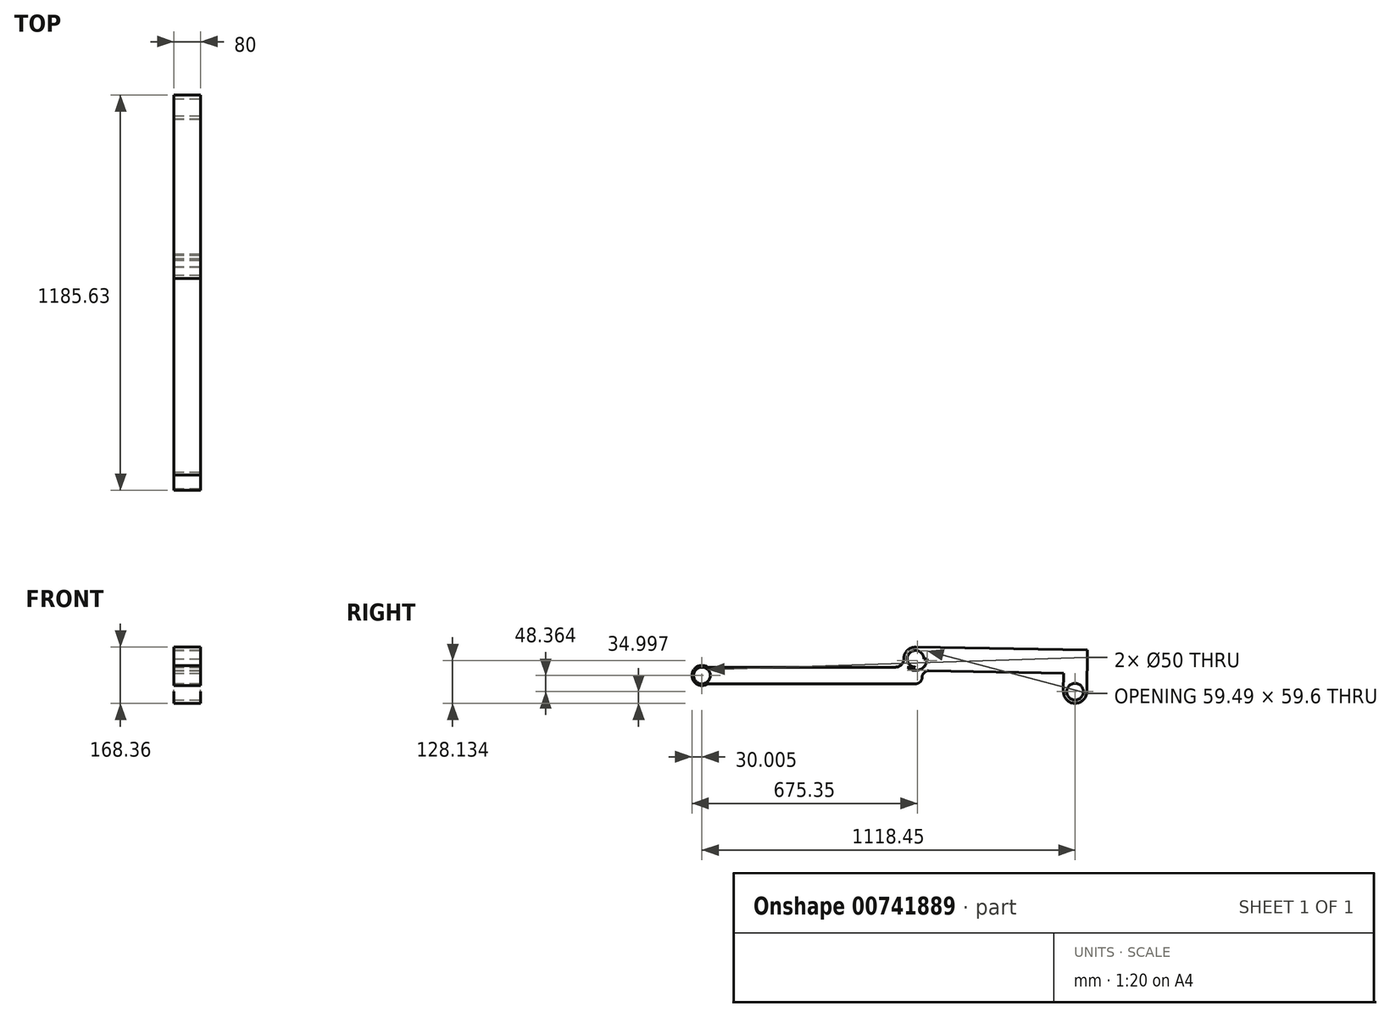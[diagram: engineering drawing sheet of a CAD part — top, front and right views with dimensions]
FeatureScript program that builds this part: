
annotation { "Feature Type Name" : "Feature", "Feature Type Description" : "" }
export const myFeature = defineFeature(function(context is Context, id is Id, definition is map)
    precondition{}
    {
        {
            var Q0;
            Q0=qCreatedBy(makeId("Right.planeOp"),FACE);
            var sketch = newSketch(context, id + "F0", { "sketchPlane" : qUnion([Q0])});
            skCircle(sketch, "E0", {"center": v(0, 0) * mm, "radius": 25 * mm});
            skLineSegment(sketch, "E1", {"start": v(0, -25) * mm, "end": v(-640, -25) * mm});
            skCircle(sketch, "E2", {"center": v(-640.1, -50) * mm, "radius": 25 * mm});
            skCircle(sketch, "E3", {"center": v(0, 0) * mm, "radius": 35 * mm});
            skArc(sketch, "E4", {"start": v(-35, 0) * mm, "mid": v(-42.32, -17.68) * mm, "end": v(-60, -25) * mm});
            skCircle(sketch, "E5", {"center": v(-640.1, -50) * mm, "radius": 30 * mm});
            skLineSegment(sketch, "E6", {"start": v(0, 0) * mm, "end": v(514.92, -8.99) * mm});
            skLineSegment(sketch, "E7", {"start": v(0, 0) * mm, "end": v(0, -25) * mm});
            skLineSegment(sketch, "E8", {"start": v(515.53, 26) * mm, "end": v(0.61, 35) * mm});
            skLineSegment(sketch, "E9", {"start": v(515.53, 26) * mm, "end": v(513.35, -98.97) * mm});
            skLineSegment(sketch, "E10", {"start": v(443.36, -97.75) * mm, "end": v(444.32, -42.76) * mm});
            skLineSegment(sketch, "E11", {"start": v(444.32, -42.76) * mm, "end": v(-0.61, -35) * mm});
            skArc(sketch, "E12", {"start": v(513.35, -98.97) * mm, "mid": v(477.75, -133.36) * mm, "end": v(443.36, -97.75) * mm});
            skCircle(sketch, "E13", {"center": v(478.36, -98.36) * mm, "radius": 25 * mm});
            skLineSegment(sketch, "E14", {"start": v(-640.1, -75) * mm, "end": v(-0.1, -75) * mm});
            skLineSegment(sketch, "E15", {"start": v(-0.1, -75) * mm, "end": v(-0.61, -35) * mm});
            skArc(sketch, "E16", {"start": v(-0.1, -75) * mm, "mid": v(20, -54.71) * mm, "end": v(-0.66, -35) * mm});
            skPoint(sketch, "E16.centerSnap0", {"position": v(-0.35, -55) * mm});
            skArc(sketch, "E17", {"start": v(39, -35.69) * mm, "mid": v(25.6, -41.5) * mm, "end": v(20, -55) * mm});
            skSolve(sketch);
        }
        {
            var Q0;
            {var subQ8=sQuery(id+"F0.wireOp",EDGE,"E10");Q0=makeQuery(id+"F0.imprint","IMPRINT",FACE,{"disambiguationData":[TD([[makeQuery(id+"F0.imprint","IMPRINT",EDGE,{"derivedFrom":subQ8}),-1.0]])]});}
            var Q1;
            {var subQ0=sQuery(id+"F0.wireOp",EDGE,"E8");Q1=makeQuery(id+"F0.imprint","IMPRINT",FACE,{"disambiguationData":[TD([[makeQuery(id+"F0.imprint","IMPRINT",EDGE,{"derivedFrom":subQ0}),1.0]])]});}
            var Q2;
            {var subQ0=sQuery(id+"F0.wireOp",EDGE,"E3");var subQ2=sQuery(id+"F0.wireOp",EDGE,"E16");var subQ10=makeQuery(id+"F0.imprint","INTERSECT",VERTEX,{"disambiguationData":[OD(1.0)],"derivedFrom":[subQ0,subQ2]});Q2=makeQuery(id+"F0.imprint","IMPRINT",FACE,{"disambiguationData":[TD([[makeQuery(id+"F0.imprint","IMPRINT",EDGE,{"disambiguationData":[TD([[subQ10,-1.0]])],"derivedFrom":subQ0}),1.0]])]});}
            var Q3;
            {var subQ0=sQuery(id+"F0.wireOp",EDGE,"E3");var subQ1=makeQuery(id+"F0.imprint","INTERSECT",VERTEX,{"derivedFrom":[subQ0,sQuery(id+"F0.wireOp",EDGE,"E4")]});Q3=makeQuery(id+"F0.imprint","IMPRINT",FACE,{"disambiguationData":[TD([[makeQuery(id+"F0.imprint","IMPRINT",EDGE,{"disambiguationData":[TD([[subQ1,1.0]])],"derivedFrom":subQ0}),1.0]])]});}
            var Q4;
            Q4 = qSketchRegion(id + "F0", true);
            var Q5;
            {var subQ0=sQuery(id+"F0.wireOp",EDGE,"E16");var subQ2=sQuery(id+"F0.wireOp",EDGE,"E11");var subQ3=makeQuery(id+"F0.imprint","INTERSECT",VERTEX,{"disambiguationData":[OD(0.0)],"derivedFrom":[subQ2,subQ0]});Q5=makeQuery(id+"F0.imprint","IMPRINT",FACE,{"disambiguationData":[TD([[makeQuery(id+"F0.imprint","IMPRINT",EDGE,{"disambiguationData":[TD([[subQ3,-1.0]])],"derivedFrom":subQ2}),1.0]])]});}
            var Q6;
            {var subQ0=sQuery(id+"F0.wireOp",EDGE,"E17");Q6=makeQuery(id+"F0.imprint","IMPRINT",FACE,{"disambiguationData":[TD([[makeQuery(id+"F0.imprint","IMPRINT",EDGE,{"derivedFrom":subQ0}),-1.0]])]});}
            var Q7;
            {var subQ0=sQuery(id+"F0.wireOp",EDGE,"E4");Q7=makeQuery(id+"F0.imprint","IMPRINT",FACE,{"disambiguationData":[TD([[makeQuery(id+"F0.imprint","IMPRINT",EDGE,{"derivedFrom":subQ0}),1.0]])]});}
            var Q8;
            {var subQ1=sQuery(id+"F0.wireOp",EDGE,"E1");var subQ9=makeQuery(id+"F0.imprint","INTERSECT",VERTEX,{"derivedFrom":[subQ1,sQuery(id+"F0.wireOp",EDGE,"E4")]});Q8=makeQuery(id+"F0.imprint","IMPRINT",FACE,{"disambiguationData":[TD([[makeQuery(id+"F0.imprint","IMPRINT",EDGE,{"disambiguationData":[TD([[subQ9,1.0]])],"derivedFrom":subQ1}),1.0]])]});}
            var Q9;
            {var subQ0=sQuery(id+"F0.wireOp",EDGE,"E2");var subQ1=sQuery(id+"F0.wireOp",EDGE,"E1");var subQ2=makeQuery(id+"F0.imprint","INTERSECT",VERTEX,{"derivedFrom":[subQ1,subQ0]});Q9=makeQuery(id+"F0.imprint","IMPRINT",FACE,{"disambiguationData":[TD([[makeQuery(id+"F0.imprint","IMPRINT",EDGE,{"disambiguationData":[TD([[subQ2,1.0]])],"derivedFrom":subQ1}),1.0]])]});}
            var Q10;
            {var subQ0=sQuery(id+"F0.wireOp",EDGE,"E2");var subQ1=sQuery(id+"F0.wireOp",EDGE,"E1");var subQ2=makeQuery(id+"F0.imprint","INTERSECT",VERTEX,{"derivedFrom":[subQ1,subQ0]});Q10=makeQuery(id+"F0.imprint","IMPRINT",FACE,{"disambiguationData":[TD([[makeQuery(id+"F0.imprint","IMPRINT",EDGE,{"disambiguationData":[TD([[subQ2,1.0]])],"derivedFrom":subQ1}),-1.0]])]});}
            extrude(context, id + "F1", {"entities" : qUnion([Q0, Q1, Q2, Q3, Q4, Q5, Q6, Q7, Q8, Q9, Q10]), "oppositeDirection" : true, "depth" : 80 * mm, "offsetDistance" : 25 * mm});
        }
    });
